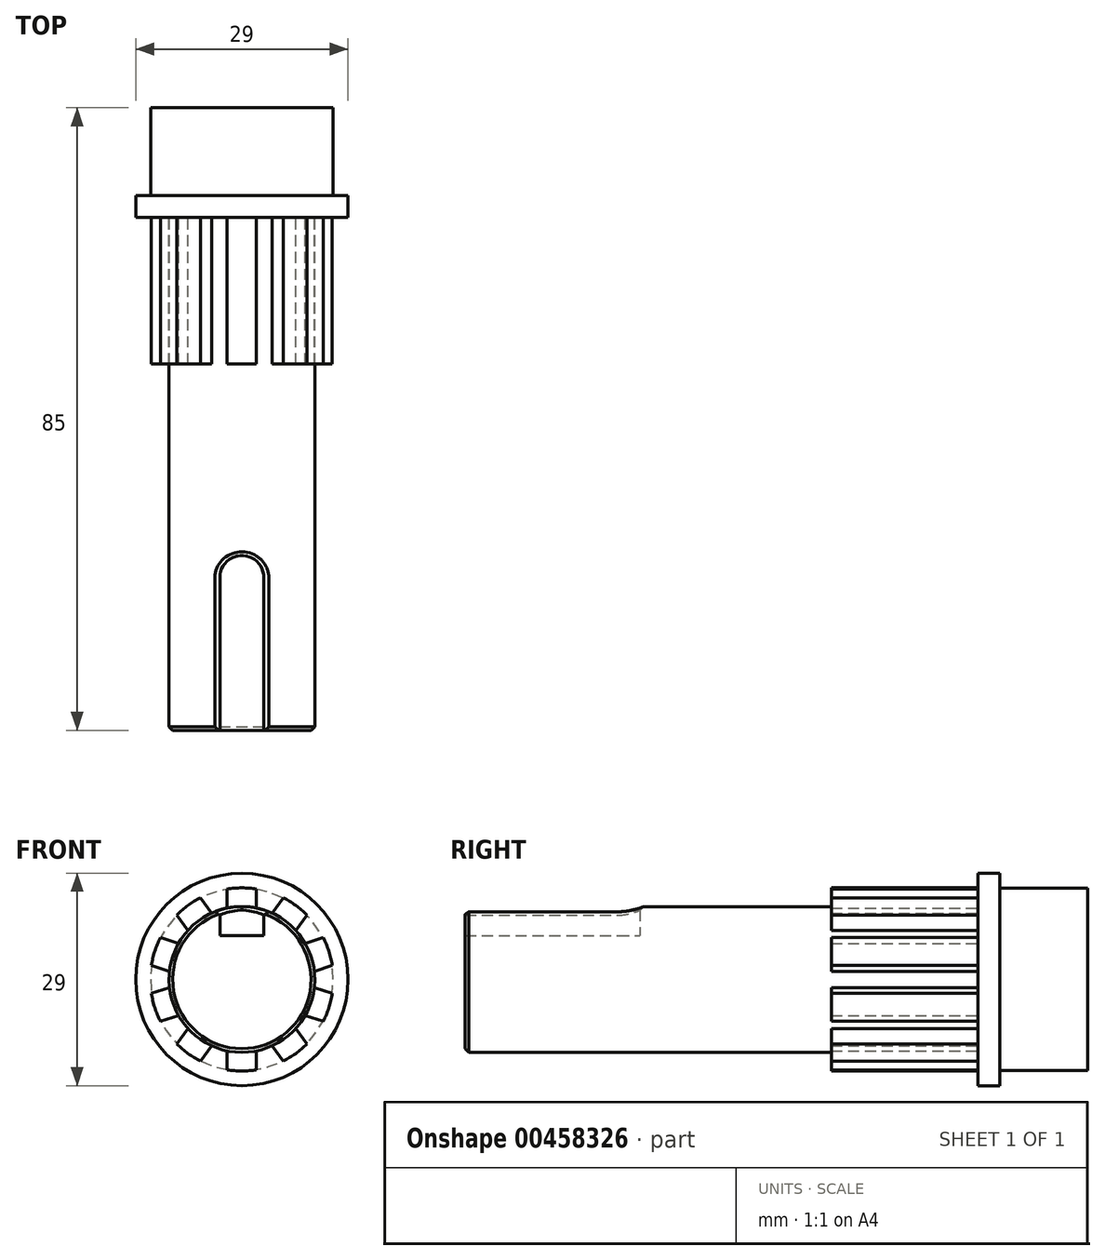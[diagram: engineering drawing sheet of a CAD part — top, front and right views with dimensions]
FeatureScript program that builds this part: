
annotation { "Feature Type Name" : "Feature", "Feature Type Description" : "" }
export const myFeature = defineFeature(function(context is Context, id is Id, definition is map)
    precondition{}
    {
        {
            var Q0;
            Q0=qCreatedBy(makeId("Front.planeOp"),FACE);
            var sketch = newSketch(context, id + "F0", { "sketchPlane" : qUnion([Q0])});
            skCircle(sketch, "E0", {"center": v(0, 0) * mm, "radius": 9.95 * mm});
            skSolve(sketch);
        }
        {
            var Q0;
            Q0 = qSketchRegion(id + "F0", true);
            var Q1;
            Q1=makeQuery(id+"F0.imprint","IMPRINT",FACE,{"disambiguationData":[TD([[makeQuery(id+"F0.imprint","IMPRINT",EDGE,{"derivedFrom":sQuery(id+"F0.wireOp",EDGE,"E0")}),1.0]])]});
            extrude(context, id + "F1", {"entities" : qUnion([Q0, Q1]), "depth" : 70 * mm});
        }
        {
            var Q0;
            Q0=qCreatedBy(makeId("Front.planeOp"),FACE);
            var sketch = newSketch(context, id + "F2", { "sketchPlane" : qUnion([Q0])});
            skCircle(sketch, "E1", {"center": v(0, 0) * mm, "radius": 14.5 * mm});
            skSolve(sketch);
        }
        {
            var Q0;
            Q0 = qSketchRegion(id + "F2", true);
            var Q1;
            Q1=makeQuery(id+"F2.imprint","IMPRINT",FACE,{"disambiguationData":[TD([[makeQuery(id+"F2.imprint","IMPRINT",EDGE,{"derivedFrom":sQuery(id+"F2.wireOp",EDGE,"E1")}),1.0]])]});
            extrude(context, id + "F3", {"entities" : qUnion([Q0, Q1]), "operationType" : NewBodyOperationType.ADD, "depth" : -3 * mm});
        }
        {
            var Q0;
            Q0=makeQuery(id+"F3.opExtrude","CAP_FACE",FACE,{"disambiguationData":[OSD([sQuery(id+"F2.wireOp",EDGE,"E1")])],"isStart":false});
            var sketch = newSketch(context, id + "F4", { "sketchPlane" : qUnion([Q0])});
            skCircle(sketch, "E2", {"center": v(0, 0) * mm, "radius": 12.45 * mm});
            skSolve(sketch);
        }
        {
            var Q0;
            Q0=makeQuery(id+"F4.imprint","IMPRINT",FACE,{"disambiguationData":[TD([[makeQuery(id+"F4.imprint","IMPRINT",EDGE,{"derivedFrom":sQuery(id+"F4.wireOp",EDGE,"E2")}),1.0]])]});
            extrude(context, id + "F5", {"entities" : qUnion([Q0]), "operationType" : NewBodyOperationType.ADD, "depth" : 12 * mm});
        }
        {
            var Q0;
            Q0=makeQuery(id+"F3.opExtrude","CAP_FACE",FACE,{"disambiguationData":[OSD([sQuery(id+"F2.wireOp",EDGE,"E1")])],"isStart":true});
            var sketch = newSketch(context, id + "F6", { "sketchPlane" : qUnion([Q0])});
            skArc(sketch, "E3", {"start": v(2, 12.34) * mm, "mid": v(0, 12.5) * mm, "end": v(-2, 12.34) * mm});
            skLineSegment(sketch, "E4", {"start": v(-2, 12.34) * mm, "end": v(-2, 8) * mm});
            skLineSegment(sketch, "E5", {"start": v(-2, 8) * mm, "end": v(2, 8) * mm});
            skLineSegment(sketch, "E6", {"start": v(2, 8) * mm, "end": v(2, 12.34) * mm});
            skLineSegment(sketch, "E7.1.0", {"start": v(-8.87, 8.8) * mm, "end": v(-6.32, 5.3) * mm});
            skLineSegment(sketch, "E7.1.1", {"start": v(-3.08, 7.65) * mm, "end": v(-5.63, 11.16) * mm});
            skArc(sketch, "E7.1.2", {"start": v(-5.63, 11.16) * mm, "mid": v(-7.35, 10.11) * mm, "end": v(-8.87, 8.8) * mm});
            skLineSegment(sketch, "E7.2.0", {"start": v(-12.35, 1.91) * mm, "end": v(-8.23, 0.57) * mm});
            skLineSegment(sketch, "E7.2.1", {"start": v(-7, 4.37) * mm, "end": v(-11.12, 5.72) * mm});
            skArc(sketch, "E7.2.2", {"start": v(-11.12, 5.72) * mm, "mid": v(-11.89, 3.86) * mm, "end": v(-12.35, 1.91) * mm});
            skLineSegment(sketch, "E7.3.0", {"start": v(-11.12, -5.72) * mm, "end": v(-7, -4.37) * mm});
            skLineSegment(sketch, "E7.3.1", {"start": v(-8.23, -0.57) * mm, "end": v(-12.35, -1.91) * mm});
            skArc(sketch, "E7.3.2", {"start": v(-12.35, -1.91) * mm, "mid": v(-11.89, -3.86) * mm, "end": v(-11.12, -5.72) * mm});
            skLineSegment(sketch, "E7.4.0", {"start": v(-5.63, -11.16) * mm, "end": v(-3.08, -7.65) * mm});
            skLineSegment(sketch, "E7.4.1", {"start": v(-6.32, -5.3) * mm, "end": v(-8.87, -8.8) * mm});
            skArc(sketch, "E7.4.2", {"start": v(-8.87, -8.8) * mm, "mid": v(-7.35, -10.11) * mm, "end": v(-5.63, -11.16) * mm});
            skLineSegment(sketch, "E7.5.0", {"start": v(2, -12.34) * mm, "end": v(2, -8) * mm});
            skLineSegment(sketch, "E7.5.1", {"start": v(-2, -8) * mm, "end": v(-2, -12.34) * mm});
            skArc(sketch, "E7.5.2", {"start": v(-2, -12.34) * mm, "mid": v(0, -12.5) * mm, "end": v(2, -12.34) * mm});
            skLineSegment(sketch, "E7.6.0", {"start": v(8.87, -8.8) * mm, "end": v(6.32, -5.3) * mm});
            skLineSegment(sketch, "E7.6.1", {"start": v(3.08, -7.65) * mm, "end": v(5.63, -11.16) * mm});
            skArc(sketch, "E7.6.2", {"start": v(5.63, -11.16) * mm, "mid": v(7.35, -10.11) * mm, "end": v(8.87, -8.8) * mm});
            skLineSegment(sketch, "E7.7.0", {"start": v(12.35, -1.91) * mm, "end": v(8.23, -0.57) * mm});
            skLineSegment(sketch, "E7.7.1", {"start": v(7, -4.37) * mm, "end": v(11.12, -5.72) * mm});
            skArc(sketch, "E7.7.2", {"start": v(11.12, -5.72) * mm, "mid": v(11.89, -3.86) * mm, "end": v(12.35, -1.91) * mm});
            skLineSegment(sketch, "E7.8.0", {"start": v(11.12, 5.72) * mm, "end": v(7, 4.37) * mm});
            skLineSegment(sketch, "E7.8.1", {"start": v(8.23, 0.57) * mm, "end": v(12.35, 1.91) * mm});
            skArc(sketch, "E7.8.2", {"start": v(12.35, 1.91) * mm, "mid": v(11.89, 3.86) * mm, "end": v(11.12, 5.72) * mm});
            skLineSegment(sketch, "E7.9.0", {"start": v(5.63, 11.16) * mm, "end": v(3.08, 7.65) * mm});
            skLineSegment(sketch, "E7.9.1", {"start": v(6.32, 5.3) * mm, "end": v(8.87, 8.8) * mm});
            skArc(sketch, "E7.9.2", {"start": v(8.87, 8.8) * mm, "mid": v(7.35, 10.11) * mm, "end": v(5.63, 11.16) * mm});
            skSolve(sketch);
        }
        {
            var Q0;
            {var subQ0=sQuery(id+"F6.wireOp",EDGE,"E3");Q0=makeQuery(id+"F6.imprint","IMPRINT",FACE,{"disambiguationData":[TD([[makeQuery(id+"F6.imprint","IMPRINT",EDGE,{"derivedFrom":subQ0}),1.0]])]});}
            var Q1;
            {var subQ0=sQuery(id+"F6.wireOp",EDGE,"E7.1.2");Q1=makeQuery(id+"F6.imprint","IMPRINT",FACE,{"disambiguationData":[TD([[makeQuery(id+"F6.imprint","IMPRINT",EDGE,{"derivedFrom":subQ0}),1.0]])]});}
            var Q2;
            {var subQ0=sQuery(id+"F6.wireOp",EDGE,"E7.2.2");Q2=makeQuery(id+"F6.imprint","IMPRINT",FACE,{"disambiguationData":[TD([[makeQuery(id+"F6.imprint","IMPRINT",EDGE,{"derivedFrom":subQ0}),1.0]])]});}
            var Q3;
            {var subQ0=sQuery(id+"F6.wireOp",EDGE,"E7.3.2");Q3=makeQuery(id+"F6.imprint","IMPRINT",FACE,{"disambiguationData":[TD([[makeQuery(id+"F6.imprint","IMPRINT",EDGE,{"derivedFrom":subQ0}),1.0]])]});}
            var Q4;
            {var subQ0=sQuery(id+"F6.wireOp",EDGE,"E7.4.2");Q4=makeQuery(id+"F6.imprint","IMPRINT",FACE,{"disambiguationData":[TD([[makeQuery(id+"F6.imprint","IMPRINT",EDGE,{"derivedFrom":subQ0}),1.0]])]});}
            var Q5;
            {var subQ0=sQuery(id+"F6.wireOp",EDGE,"E7.5.2");Q5=makeQuery(id+"F6.imprint","IMPRINT",FACE,{"disambiguationData":[TD([[makeQuery(id+"F6.imprint","IMPRINT",EDGE,{"derivedFrom":subQ0}),1.0]])]});}
            var Q6;
            {var subQ0=sQuery(id+"F6.wireOp",EDGE,"E7.6.2");Q6=makeQuery(id+"F6.imprint","IMPRINT",FACE,{"disambiguationData":[TD([[makeQuery(id+"F6.imprint","IMPRINT",EDGE,{"derivedFrom":subQ0}),1.0]])]});}
            var Q7;
            {var subQ0=sQuery(id+"F6.wireOp",EDGE,"E7.7.2");Q7=makeQuery(id+"F6.imprint","IMPRINT",FACE,{"disambiguationData":[TD([[makeQuery(id+"F6.imprint","IMPRINT",EDGE,{"derivedFrom":subQ0}),1.0]])]});}
            var Q8;
            {var subQ0=sQuery(id+"F6.wireOp",EDGE,"E7.8.2");Q8=makeQuery(id+"F6.imprint","IMPRINT",FACE,{"disambiguationData":[TD([[makeQuery(id+"F6.imprint","IMPRINT",EDGE,{"derivedFrom":subQ0}),1.0]])]});}
            var Q9;
            {var subQ0=sQuery(id+"F6.wireOp",EDGE,"E7.9.2");Q9=makeQuery(id+"F6.imprint","IMPRINT",FACE,{"disambiguationData":[TD([[makeQuery(id+"F6.imprint","IMPRINT",EDGE,{"derivedFrom":subQ0}),1.0]])]});}
            extrude(context, id + "F7", {"entities" : qUnion([Q0, Q1, Q2, Q3, Q4, Q5, Q6, Q7, Q8, Q9]), "operationType" : NewBodyOperationType.ADD, "depth" : 20 * mm});
        }
        {
            var Q0;
            Q0=qCreatedBy(makeId("Top.planeOp"),FACE);
            cPlane(context, id + "F8", {"entities" : qUnion([Q0]), "cplaneType" : CPlaneType.OFFSET, "offset" : 6 * mm, "width" : 150 * mm, "height" : 150 * mm});
        }
        {
            var Q0;
            Q0=qCreatedBy(id+"F8.planeOp",FACE);
            var sketch = newSketch(context, id + "F9", { "sketchPlane" : qUnion([Q0])});
            skLineSegment(sketch, "E8.bottom", {"start": v(0, -70.12) * mm, "end": v(3, -70.12) * mm});
            skLineSegment(sketch, "E8.right", {"start": v(3, -70.12) * mm, "end": v(3, -49.12) * mm});
            skLineSegment(sketch, "E9.top", {"start": v(0, -70.12) * mm, "end": v(-3, -70.12) * mm});
            skLineSegment(sketch, "E9.left", {"start": v(0, -49.12) * mm, "end": v(0, -70.12) * mm});
            skLineSegment(sketch, "E9.right", {"start": v(-3, -49.12) * mm, "end": v(-3, -70.12) * mm});
            skArc(sketch, "E10", {"start": v(3, -49.12) * mm, "mid": v(0, -46.12) * mm, "end": v(-3, -49.12) * mm});
            skSolve(sketch);
        }
        {
            var Q0;
            Q0 = qSketchRegion(id + "F9", true);
            extrude(context, id + "F10", {"entities" : qUnion([Q0]), "operationType" : NewBodyOperationType.REMOVE, "depth" : 25 * mm});
        }
        {
            var Q0;
            Q0=makeQuery(id+"F10.boolean.opBoolean","INTERSECT",EDGE,{"derivedFrom":[makeQuery(id+"F1.opExtrude","SWEPT_FACE",FACE,{"disambiguationData":[OSD([sQuery(id+"F0.wireOp",EDGE,"E0")])]}),makeQuery(id+"F10.opExtrude","SWEPT_FACE",FACE,{"disambiguationData":[OSD([sQuery(id+"F9.wireOp",EDGE,"E9.right")])]})]});
            var Q1;
            Q1=makeQuery(id+"F1.opExtrude","CAP_EDGE",EDGE,{"disambiguationData":[OSD([sQuery(id+"F0.wireOp",EDGE,"E0")])],"isStart":false});
            chamfer(context, id + "F11", {"entities" : qUnion([Q0, Q1]), "width" : 0.5 * mm, "tangentPropagation" : true});
        }
    });
